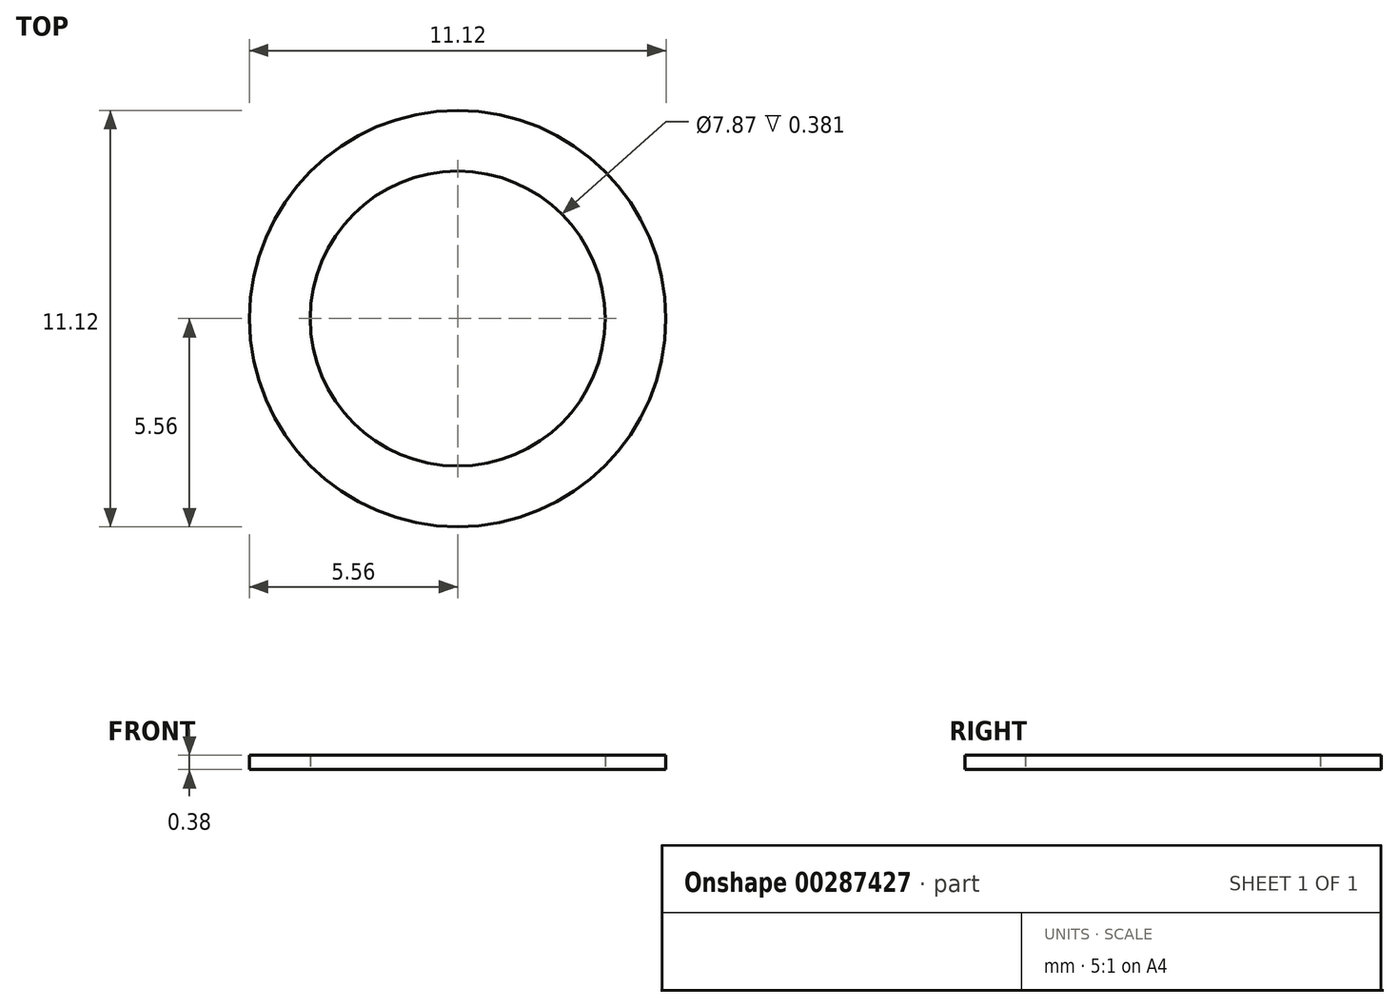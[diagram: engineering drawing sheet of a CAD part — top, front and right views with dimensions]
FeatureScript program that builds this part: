
annotation { "Feature Type Name" : "Feature", "Feature Type Description" : "" }
export const myFeature = defineFeature(function(context is Context, id is Id, definition is map)
    precondition{}
    {
        {
            var Q0;
            Q0=qCreatedBy(makeId("Top.planeOp"),FACE);
            var sketch = newSketch(context, id + "F0", { "sketchPlane" : qUnion([Q0])});
            skCircle(sketch, "E0", {"center": v(0, 0) * mm, "radius": 3.94 * mm});
            skCircle(sketch, "E1", {"center": v(0, 0) * mm, "radius": 5.56 * mm});
            skSolve(sketch);
        }
        {
            var Q0;
            Q0=makeQuery(id+"F0.imprint","IMPRINT",FACE,{"disambiguationData":[TD([[makeQuery(id+"F0.imprint","IMPRINT",EDGE,{"derivedFrom":sQuery(id+"F0.wireOp",EDGE,"E0")}),-1.0]])]});
            extrude(context, id + "F1", {"entities" : qUnion([Q0]), "depth" : 0.38 * mm});
        }
    });
